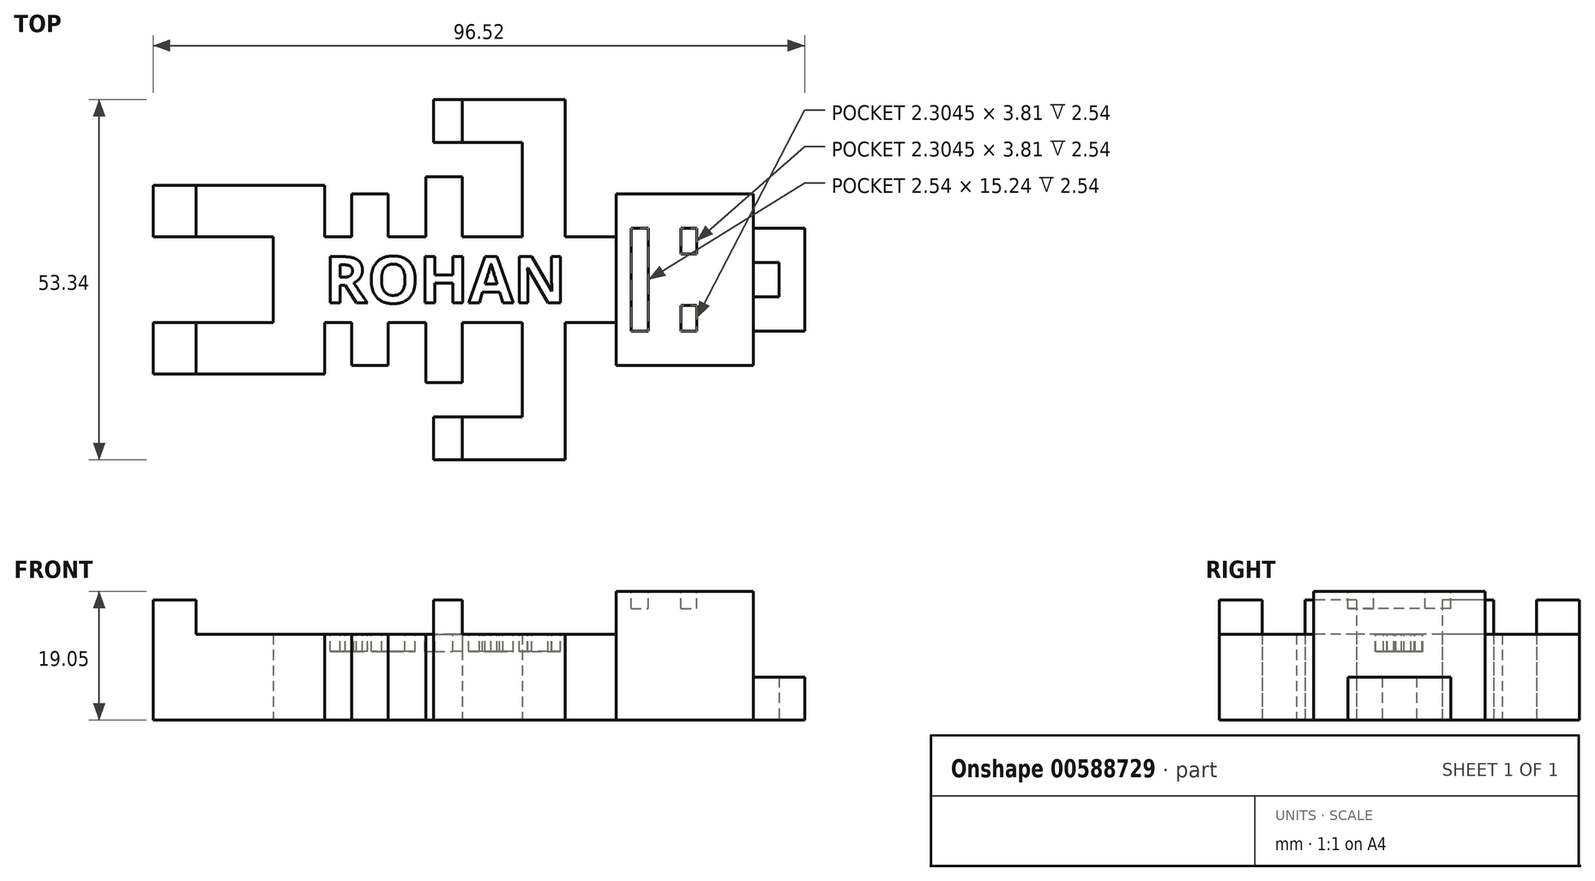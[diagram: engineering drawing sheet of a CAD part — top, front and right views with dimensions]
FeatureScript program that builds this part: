
annotation { "Feature Type Name" : "Feature", "Feature Type Description" : "" }
export const myFeature = defineFeature(function(context is Context, id is Id, definition is map)
    precondition{}
    {
        {
            var Q0;
            Q0=qCreatedBy(makeId("Top.planeOp"),FACE);
            var sketch = newSketch(context, id + "F0", { "sketchPlane" : qUnion([Q0])});
            skLineSegment(sketch, "E0.bottom", {"start": v(23.65, 12.7) * mm, "end": v(43.97, 12.7) * mm});
            skLineSegment(sketch, "E0.top", {"start": v(23.65, -12.7) * mm, "end": v(43.97, -12.7) * mm});
            skLineSegment(sketch, "E0.left", {"start": v(23.65, 12.7) * mm, "end": v(23.65, -12.7) * mm});
            skLineSegment(sketch, "E0.right", {"start": v(43.97, 12.7) * mm, "end": v(43.97, -12.7) * mm});
            skSolve(sketch);
        }
        {
            var Q0;
            Q0 = qSketchRegion(id + "F0", true);
            extrude(context, id + "F1", {"entities" : qUnion([Q0]), "depth" : 19.05 * mm, "offsetDistance" : 25.4 * mm});
        }
        {
            var Q0;
            Q0=qCreatedBy(makeId("Top.planeOp"),FACE);
            var sketch = newSketch(context, id + "F2", { "sketchPlane" : qUnion([Q0])});
            skLineSegment(sketch, "E1.left", {"start": v(-27.15, 6.35) * mm, "end": v(-27.15, -6.35) * mm});
            skLineSegment(sketch, "E1.right", {"start": v(23.65, 6.35) * mm, "end": v(23.65, -6.35) * mm});
            skLineSegment(sketch, "E2.right", {"start": v(-19.53, 13.97) * mm, "end": v(-19.53, 6.35) * mm});
            skLineSegment(sketch, "E3.bottom", {"start": v(-44.93, 13.97) * mm, "end": v(-19.53, 13.97) * mm});
            skLineSegment(sketch, "E3.top", {"start": v(-44.93, 6.35) * mm, "end": v(-27.15, 6.35) * mm});
            skLineSegment(sketch, "E3.left", {"start": v(-44.93, 13.97) * mm, "end": v(-44.93, 6.35) * mm});
            skLineSegment(sketch, "E4.bottom", {"start": v(-27.15, -6.35) * mm, "end": v(-44.93, -6.35) * mm});
            skLineSegment(sketch, "E4.top", {"start": v(-19.53, -13.97) * mm, "end": v(-44.93, -13.97) * mm});
            skLineSegment(sketch, "E4.right", {"start": v(-44.93, -6.35) * mm, "end": v(-44.93, -13.97) * mm});
            skLineSegment(sketch, "E5", {"start": v(-19.53, -6.35) * mm, "end": v(23.65, -6.35) * mm});
            skLineSegment(sketch, "E6", {"start": v(-19.53, -6.35) * mm, "end": v(-19.53, -13.97) * mm});
            skLineSegment(sketch, "E7", {"start": v(-19.53, 6.35) * mm, "end": v(23.65, 6.35) * mm});
            skLineSegment(sketch, "E8.bottom", {"start": v(-4.54, 15.24) * mm, "end": v(0.84, 15.24) * mm});
            skLineSegment(sketch, "E8.top", {"start": v(-4.54, -15.24) * mm, "end": v(0.84, -15.24) * mm});
            skLineSegment(sketch, "E8.left", {"start": v(-4.54, 15.24) * mm, "end": v(-4.54, -15.24) * mm});
            skLineSegment(sketch, "E8.right", {"start": v(0.84, 15.24) * mm, "end": v(0.84, -15.24) * mm});
            skLineSegment(sketch, "E9.bottom", {"start": v(9.79, 26.67) * mm, "end": v(16.14, 26.67) * mm});
            skLineSegment(sketch, "E9.top", {"start": v(9.79, -26.67) * mm, "end": v(16.14, -26.67) * mm});
            skLineSegment(sketch, "E9.left", {"start": v(9.79, 26.67) * mm, "end": v(9.79, -26.67) * mm});
            skLineSegment(sketch, "E9.right", {"start": v(16.14, 26.67) * mm, "end": v(16.14, -26.67) * mm});
            skLineSegment(sketch, "E10.bottom", {"start": v(-3.38, 26.67) * mm, "end": v(16.14, 26.67) * mm});
            skLineSegment(sketch, "E10.top", {"start": v(-3.38, 20.32) * mm, "end": v(16.14, 20.32) * mm});
            skLineSegment(sketch, "E10.left", {"start": v(-3.38, 26.67) * mm, "end": v(-3.38, 20.32) * mm});
            skLineSegment(sketch, "E10.right", {"start": v(16.14, 26.67) * mm, "end": v(16.14, 20.32) * mm});
            skLineSegment(sketch, "E11.bottom", {"start": v(-3.38, -20.32) * mm, "end": v(16.14, -20.32) * mm});
            skLineSegment(sketch, "E11.top", {"start": v(-3.38, -26.67) * mm, "end": v(16.14, -26.67) * mm});
            skLineSegment(sketch, "E11.left", {"start": v(-3.38, -20.32) * mm, "end": v(-3.38, -26.67) * mm});
            skLineSegment(sketch, "E11.right", {"start": v(16.14, -20.32) * mm, "end": v(16.14, -26.67) * mm});
            skLineSegment(sketch, "E12.bottom", {"start": v(-44.93, 13.97) * mm, "end": v(-38.27, 13.97) * mm});
            skLineSegment(sketch, "E12.top", {"start": v(-44.93, 6.35) * mm, "end": v(-38.27, 6.35) * mm});
            skLineSegment(sketch, "E12.right", {"start": v(-38.27, 13.97) * mm, "end": v(-38.27, 6.35) * mm});
            skLineSegment(sketch, "E13.bottom", {"start": v(-44.93, -6.35) * mm, "end": v(-38.27, -6.35) * mm});
            skLineSegment(sketch, "E13.top", {"start": v(-44.93, -13.97) * mm, "end": v(-38.27, -13.97) * mm});
            skLineSegment(sketch, "E13.right", {"start": v(-38.27, -6.35) * mm, "end": v(-38.27, -13.97) * mm});
            skLineSegment(sketch, "E14.bottom", {"start": v(43.97, 7.62) * mm, "end": v(51.6, 7.62) * mm});
            skLineSegment(sketch, "E14.top", {"start": v(43.97, -7.62) * mm, "end": v(51.6, -7.62) * mm});
            skLineSegment(sketch, "E14.right", {"start": v(51.6, 7.62) * mm, "end": v(51.6, -7.62) * mm});
            skLineSegment(sketch, "E15.bottom", {"start": v(43.97, 2.54) * mm, "end": v(47.78, 2.54) * mm});
            skLineSegment(sketch, "E15.top", {"start": v(43.97, -2.54) * mm, "end": v(47.78, -2.54) * mm});
            skLineSegment(sketch, "E15.right", {"start": v(47.78, 2.54) * mm, "end": v(47.78, -2.54) * mm});
            skLineSegment(sketch, "E16", {"start": v(43.97, 7.62) * mm, "end": v(43.97, 2.54) * mm});
            skLineSegment(sketch, "E17", {"start": v(43.97, -2.54) * mm, "end": v(43.97, -7.62) * mm});
            skLineSegment(sketch, "E18.bottom", {"start": v(-15.51, 12.7) * mm, "end": v(-10.14, 12.7) * mm});
            skLineSegment(sketch, "E18.top", {"start": v(-15.51, -12.7) * mm, "end": v(-10.14, -12.7) * mm});
            skLineSegment(sketch, "E18.left", {"start": v(-15.51, 12.7) * mm, "end": v(-15.51, -12.7) * mm});
            skLineSegment(sketch, "E18.right", {"start": v(-10.14, 12.7) * mm, "end": v(-10.14, -12.7) * mm});
            skSolve(sketch);
        }
        {
            var Q0;
            Q0 = qSketchRegion(id + "F2", true);
            extrude(context, id + "F3", {"entities" : qUnion([Q0]), "operationType" : NewBodyOperationType.ADD, "depth" : 12.7 * mm, "offsetDistance" : 25.4 * mm});
        }
        {
            var Q0;
            Q0=makeQuery(id+"F3.opExtrude","CAP_FACE",FACE,{"disambiguationData":[OSD([sQuery(id+"F2.wireOp",EDGE,"E1.bottom"),sQuery(id+"F2.wireOp",EDGE,"E1.top"),sQuery(id+"F2.wireOp",EDGE,"E1.left"),sQuery(id+"F2.wireOp",EDGE,"E1.right")])],"isStart":false});
            var sketch = newSketch(context, id + "F4", { "sketchPlane" : qUnion([Q0])});
            skText(sketch, "E19", { "text": "ROHAN", "fontName": "OpenSans-Bold.ttf"});
            skLineSegment(sketch, "E20", {"start": v(-27.15, 1.62) * mm, "end": v(-19.53, 1.62) * mm, "construction": true});
            skLineSegment(sketch, "E21", {"start": v(16.03, 1.82) * mm, "end": v(23.65, 1.82) * mm, "construction": true});
            skLineSegment(sketch, "E22", {"start": v(-7.34, 6.35) * mm, "end": v(-7.34, 3.46) * mm, "construction": true});
            skLineSegment(sketch, "E23", {"start": v(-7.34, -3.46) * mm, "end": v(-7.34, -6.35) * mm, "construction": true});
            const initialGuessF4  = {"E19": [-0.01953, -0.00346, 1, 0, 0.00692]};
            skSetInitialGuess(sketch, initialGuessF4);
            skSolve(sketch);
        }
        {
            var Q0;
            Q0 = qSketchRegion(id + "F4", true);
            extrude(context, id + "F5", {"entities" : qUnion([Q0]), "operationType" : NewBodyOperationType.REMOVE, "oppositeDirection" : true, "depth" : 2.54 * mm, "offsetDistance" : 25.4 * mm});
        }
        {
            var Q0;
            {var subQ0=sQuery(id+"F2.wireOp",EDGE,"E4.right");var subQ1=sQuery(id+"F2.wireOp",EDGE,"E3.left");var subQ2=sQuery(id+"F2.wireOp",EDGE,"E11.left");var subQ3=sQuery(id+"F2.wireOp",EDGE,"E11.top");var subQ4=sQuery(id+"F2.wireOp",EDGE,"E11.bottom");var subQ5=sQuery(id+"F2.wireOp",EDGE,"E10.left");var subQ6=sQuery(id+"F2.wireOp",EDGE,"E10.top");var subQ7=sQuery(id+"F2.wireOp",EDGE,"E10.bottom");var subQ8=sQuery(id+"F2.wireOp",EDGE,"E9.left");var subQ9=sQuery(id+"F2.wireOp",EDGE,"E5");var subQ11=sQuery(id+"F2.wireOp",EDGE,"b1yj5epB-XAph-rOL2-hmb4-3anf1PWrTN1n.right");var subQ12=sQuery(id+"F2.wireOp",EDGE,"b1yj5epB-XAph-rOL2-hmb4-3anf1PWrTN1n.bottom");var subQ13=sQuery(id+"F2.wireOp",EDGE,"E7");var subQ15=sQuery(id+"F2.wireOp",EDGE,"b1yj5epB-XAph-rOL2-hmb4-3anf1PWrTN1n.left");var subQ16=sQuery(id+"F2.wireOp",EDGE,"b1yj5epB-XAph-rOL2-hmb4-3anf1PWrTN1n.top");var subQ19=sQuery(id+"F2.wireOp",EDGE,"E1.right");var subQ20=sQuery(id+"F2.wireOp",EDGE,"E9.right");var subQ21=sQuery(id+"F2.wireOp",EDGE,"E8.right");var subQ24=sQuery(id+"F2.wireOp",EDGE,"E8.left");var subQ26=sQuery(id+"F2.wireOp",EDGE,"E2.right");var subQ27=sQuery(id+"F2.wireOp",EDGE,"E6");var subQ31=sQuery(id+"F2.wireOp",EDGE,"E13.top");var subQ32=sQuery(id+"F2.wireOp",EDGE,"E4.top");var subQ33=sQuery(id+"F2.wireOp",EDGE,"E13.bottom");var subQ34=sQuery(id+"F2.wireOp",EDGE,"E4.bottom");var subQ35=sQuery(id+"F2.wireOp",EDGE,"E12.top");var subQ36=sQuery(id+"F2.wireOp",EDGE,"E3.top");var subQ37=sQuery(id+"F2.wireOp",EDGE,"E11.right");var subQ38=sQuery(id+"F2.wireOp",EDGE,"E10.right");var subQ39=sQuery(id+"F2.wireOp",EDGE,"E8.top");var subQ40=sQuery(id+"F2.wireOp",EDGE,"E8.bottom");var subQ41=sQuery(id+"F2.wireOp",EDGE,"E1.left");var subQ42=sQuery(id+"F2.wireOp",EDGE,"E12.bottom");var subQ43=sQuery(id+"F2.wireOp",EDGE,"E3.bottom");Q0=makeQuery(id+"F5.boolean.opBoolean","SPLIT",FACE,{"disambiguationData":[TD([makeQuery(id+"F1.opExtrude","SWEPT_FACE",FACE,{"disambiguationData":[OSD([sQuery(id+"F0.wireOp",EDGE,"E0.left")])]})])],"derivedFrom":makeQuery(id+"F3.opExtrude","CAP_FACE",FACE,{"disambiguationData":[OSD([subQ41,subQ19,subQ26,subQ43,subQ36,subQ34,subQ32,subQ9,subQ27,subQ13,subQ12,subQ16,subQ15,subQ11,subQ40,subQ39,subQ24,subQ21,subQ8,subQ20,subQ7,subQ6,subQ5,subQ38,subQ4,subQ3,subQ2,subQ37,subQ42,subQ35,subQ1,subQ33,subQ31,subQ0])],"isStart":false})});}
            var sketch = newSketch(context, id + "F6", { "sketchPlane" : qUnion([Q0])});
            skLineSegment(sketch, "E24.bottom", {"start": v(-44.93, 13.97) * mm, "end": v(-38.58, 13.97) * mm});
            skLineSegment(sketch, "E24.top", {"start": v(-44.93, 6.35) * mm, "end": v(-38.58, 6.35) * mm});
            skLineSegment(sketch, "E24.left", {"start": v(-44.93, 13.97) * mm, "end": v(-44.93, 6.35) * mm});
            skLineSegment(sketch, "E24.right", {"start": v(-38.58, 13.97) * mm, "end": v(-38.58, 6.35) * mm});
            skPoint(sketch, "E25.oppositeSnap0", {"position": v(-38.58, 10.16) * mm});
            skLineSegment(sketch, "E25.bottom", {"start": v(-44.93, -6.35) * mm, "end": v(-38.58, -6.35) * mm});
            skLineSegment(sketch, "E25.top", {"start": v(-44.93, -13.97) * mm, "end": v(-38.58, -13.97) * mm});
            skLineSegment(sketch, "E25.left", {"start": v(-44.93, -6.35) * mm, "end": v(-44.93, -13.97) * mm});
            skLineSegment(sketch, "E25.right", {"start": v(-38.58, -6.35) * mm, "end": v(-38.58, -13.97) * mm});
            skLineSegment(sketch, "E26.bottom", {"start": v(-3.38, 26.67) * mm, "end": v(0.84, 26.67) * mm});
            skLineSegment(sketch, "E26.top", {"start": v(-3.38, 20.32) * mm, "end": v(0.84, 20.32) * mm});
            skLineSegment(sketch, "E26.left", {"start": v(-3.38, 26.67) * mm, "end": v(-3.38, 20.32) * mm});
            skLineSegment(sketch, "E26.right", {"start": v(0.84, 26.67) * mm, "end": v(0.84, 20.32) * mm});
            skPoint(sketch, "E27.oppositeSnap0", {"position": v(0.84, 10.8) * mm});
            skLineSegment(sketch, "E27.bottom", {"start": v(-3.38, -20.32) * mm, "end": v(0.84, -20.32) * mm});
            skLineSegment(sketch, "E27.top", {"start": v(-3.38, -26.67) * mm, "end": v(0.84, -26.67) * mm});
            skLineSegment(sketch, "E27.left", {"start": v(-3.38, -20.32) * mm, "end": v(-3.38, -26.67) * mm});
            skLineSegment(sketch, "E27.right", {"start": v(0.84, -20.32) * mm, "end": v(0.84, -26.67) * mm});
            skSolve(sketch);
        }
        {
            var Q0;
            Q0 = qSketchRegion(id + "F6", true);
            extrude(context, id + "F7", {"entities" : qUnion([Q0]), "operationType" : NewBodyOperationType.ADD, "depth" : 5.08 * mm, "offsetDistance" : 25.4 * mm});
        }
        {
            var Q0;
            Q0=makeQuery(id+"F1.opExtrude","CAP_FACE",FACE,{"disambiguationData":[OSD([sQuery(id+"F0.wireOp",EDGE,"E0.bottom"),sQuery(id+"F0.wireOp",EDGE,"E0.top"),sQuery(id+"F0.wireOp",EDGE,"E0.left"),sQuery(id+"F0.wireOp",EDGE,"E0.right")])],"isStart":false});
            var sketch = newSketch(context, id + "F8", { "sketchPlane" : qUnion([Q0])});
            skLineSegment(sketch, "E28.bottom", {"start": v(25.88, 7.62) * mm, "end": v(28.42, 7.62) * mm});
            skLineSegment(sketch, "E28.top", {"start": v(25.88, -7.62) * mm, "end": v(28.42, -7.62) * mm});
            skLineSegment(sketch, "E28.left", {"start": v(25.88, 7.62) * mm, "end": v(25.88, -7.62) * mm});
            skLineSegment(sketch, "E28.right", {"start": v(28.42, 7.62) * mm, "end": v(28.42, -7.62) * mm});
            skLineSegment(sketch, "E29.bottom", {"start": v(33.28, 7.62) * mm, "end": v(35.58, 7.62) * mm});
            skLineSegment(sketch, "E29.top", {"start": v(33.28, 3.81) * mm, "end": v(35.58, 3.81) * mm});
            skLineSegment(sketch, "E29.left", {"start": v(33.28, 7.62) * mm, "end": v(33.28, 3.81) * mm});
            skLineSegment(sketch, "E29.right", {"start": v(35.58, 7.62) * mm, "end": v(35.58, 3.81) * mm});
            skPoint(sketch, "E30.firstSnap0", {"position": v(33.28, 5.72) * mm});
            skLineSegment(sketch, "E30.bottom", {"start": v(33.28, -7.62) * mm, "end": v(35.58, -7.62) * mm});
            skLineSegment(sketch, "E30.top", {"start": v(33.28, -3.81) * mm, "end": v(35.58, -3.81) * mm});
            skLineSegment(sketch, "E30.left", {"start": v(33.28, -7.62) * mm, "end": v(33.28, -3.81) * mm});
            skLineSegment(sketch, "E30.right", {"start": v(35.58, -7.62) * mm, "end": v(35.58, -3.81) * mm});
            skSolve(sketch);
        }
        {
            var Q0;
            Q0 = qSketchRegion(id + "F8", true);
            extrude(context, id + "F9", {"entities" : qUnion([Q0]), "operationType" : NewBodyOperationType.REMOVE, "oppositeDirection" : true, "depth" : 2.54 * mm, "offsetDistance" : 25.4 * mm});
        }
        {
            var Q0;
            Q0=makeQuery(id+"F3.opExtrude","SWEPT_FACE",FACE,{"disambiguationData":[OSD([sQuery(id+"F2.wireOp",EDGE,"E14.right")])]});
            var sketch = newSketch(context, id + "F10", { "sketchPlane" : qUnion([Q0])});
            skLineSegment(sketch, "E31.bottom", {"start": v(-7.62, 12.7) * mm, "end": v(7.62, 12.7) * mm});
            skLineSegment(sketch, "E31.top", {"start": v(-7.62, 6.35) * mm, "end": v(7.62, 6.35) * mm});
            skLineSegment(sketch, "E31.left", {"start": v(-7.62, 12.7) * mm, "end": v(-7.62, 6.35) * mm});
            skLineSegment(sketch, "E31.right", {"start": v(7.62, 12.7) * mm, "end": v(7.62, 6.35) * mm});
            skSolve(sketch);
        }
        {
            var Q0;
            Q0 = qSketchRegion(id + "F10", true);
            var Q1;
            Q1=makeQuery(id+"F1.opExtrude","SWEPT_FACE",FACE,{"disambiguationData":[OSD([sQuery(id+"F0.wireOp",EDGE,"E0.right")])]});
            extrude(context, id + "F11", {"entities" : qUnion([Q0]), "operationType" : NewBodyOperationType.REMOVE, "endBound" : BoundingType.UP_TO_SURFACE, "oppositeDirection" : true, "depth" : 25.4 * mm, "endBoundEntityFace" : qUnion([Q1]), "offsetDistance" : 25.4 * mm});
        }
        {
            var Q0;
            Q0 = qSketchRegion(id + "F4", true);
            extrude(context, id + "F12", {"entities" : qUnion([Q0]), "operationType" : NewBodyOperationType.REMOVE, "depth" : 2.54 * mm, "offsetDistance" : 25.4 * mm});
        }
    });
